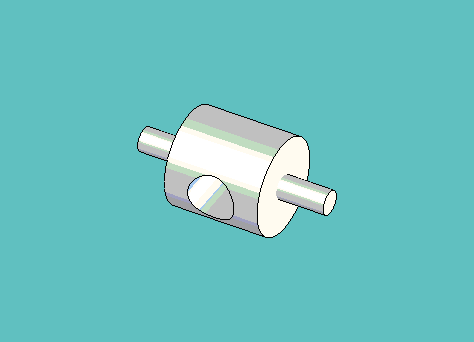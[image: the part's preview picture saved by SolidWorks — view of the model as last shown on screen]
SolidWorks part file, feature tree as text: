
SOLIDWORKS PART (.sldprt)
format: sldprt  version: not decoded by parser v0  size: 238,592 bytes
history: native  units: mm
features: sketch x4, extrude x3, material x1, cut_extrude x1 (+11 scaffold rows collapsed)
feature tree (20):
  scaffold x11  (default folders/planes/origin — collapsed)
  material  "Material <not specified>"
  sketch  "Sketch1"  dims[D1=12.7mm]
  extrude  "Extrude1"  Depth=6.35mm
  sketch  "Sketch2"  dims[D1=6.35mm]
  cut_extrude  "Cut-Extrude1"  [1 undecoded]
  sketch  "Sketch3"  dims[D1=3.175mm]
  extrude  "Extrude2"  Depth=6.35mm
  sketch  "Sketch4"
  extrude  "Extrude3"  Depth=6.35mm
decode coverage: 6 of 8 modeling features carry decoded parameters
note: 1 parameter value undecoded
note: suppression state not decoded; provenance and decode notes live in map.json
